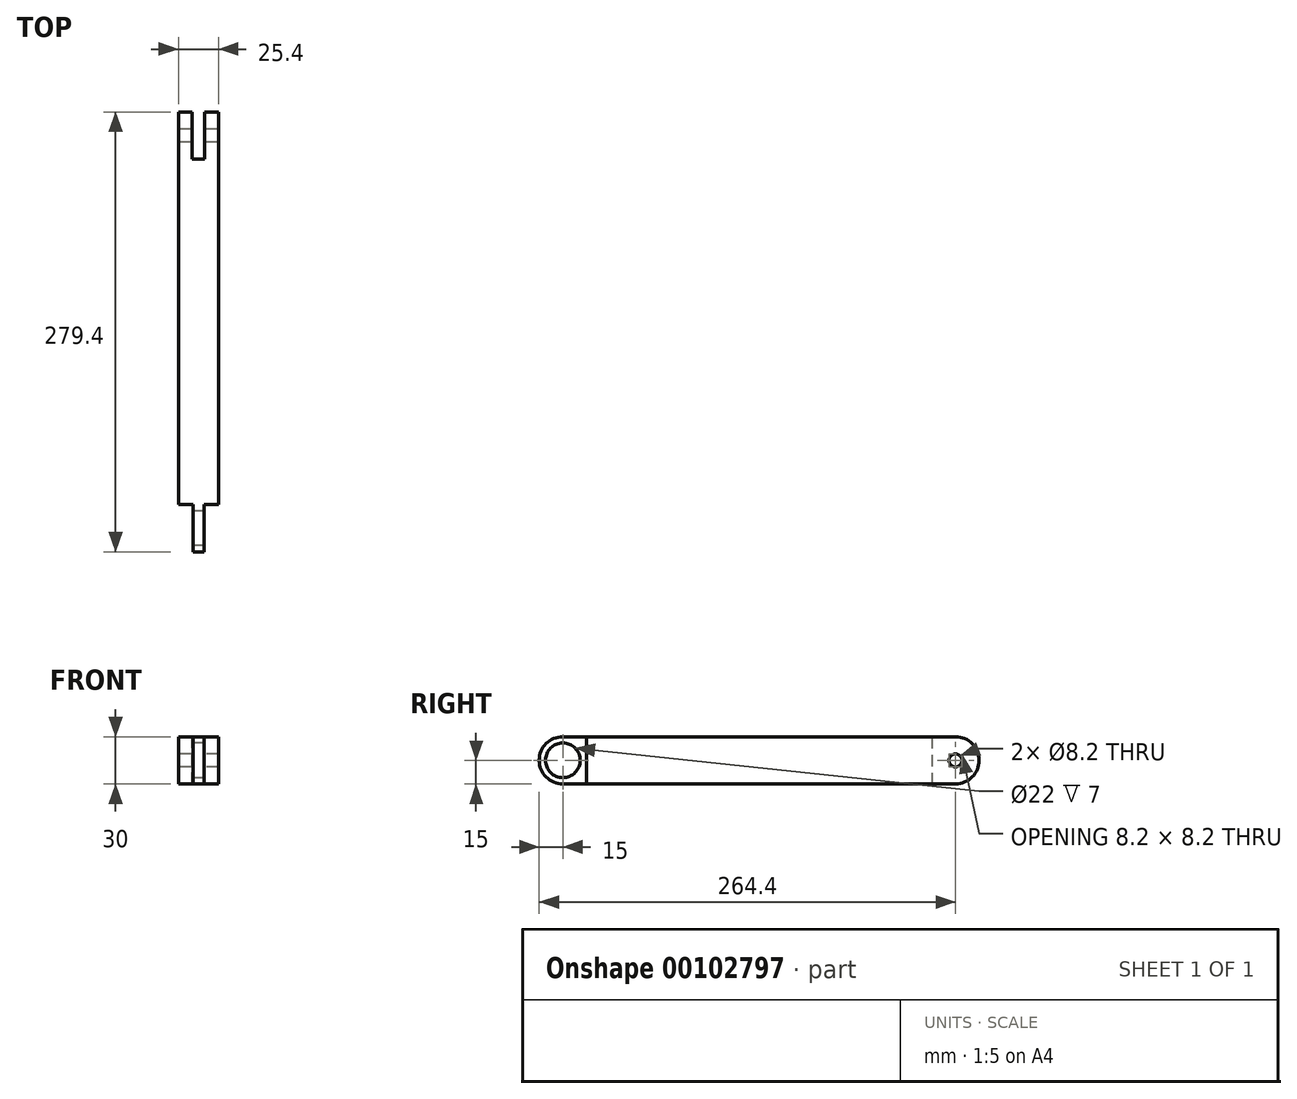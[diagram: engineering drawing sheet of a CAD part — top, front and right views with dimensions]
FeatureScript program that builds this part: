
annotation { "Feature Type Name" : "Feature", "Feature Type Description" : "" }
export const myFeature = defineFeature(function(context is Context, id is Id, definition is map)
    precondition{}
    {
        {
            var Q0;
            Q0=qCreatedBy(makeId("Top.planeOp"),FACE);
            var sketch = newSketch(context, id + "F0", { "sketchPlane" : qUnion([Q0])});
            skLineSegment(sketch, "E0", {"start": v(-12.7, 124.7) * mm, "end": v(-4, 124.7) * mm});
            skLineSegment(sketch, "E1", {"start": v(-4, 124.7) * mm, "end": v(-4, 94.7) * mm});
            skLineSegment(sketch, "E2", {"start": v(-4, 94.7) * mm, "end": v(4, 94.7) * mm});
            skLineSegment(sketch, "E3", {"start": v(4, 94.7) * mm, "end": v(4, 124.7) * mm});
            skLineSegment(sketch, "E4", {"start": v(4, 124.7) * mm, "end": v(12.7, 124.7) * mm});
            skLineSegment(sketch, "E5", {"start": v(12.7, 124.7) * mm, "end": v(12.7, -124.7) * mm});
            skLineSegment(sketch, "E6", {"start": v(12.7, -124.7) * mm, "end": v(3.5, -124.7) * mm});
            skLineSegment(sketch, "E7", {"start": v(3.5, -124.7) * mm, "end": v(3.5, -154.7) * mm});
            skLineSegment(sketch, "E8", {"start": v(3.5, -154.7) * mm, "end": v(-3.5, -154.7) * mm});
            skLineSegment(sketch, "E9", {"start": v(-3.5, -154.7) * mm, "end": v(-3.5, -124.7) * mm});
            skLineSegment(sketch, "E10", {"start": v(-3.5, -124.7) * mm, "end": v(-12.7, -124.7) * mm});
            skLineSegment(sketch, "E11", {"start": v(-12.7, -124.7) * mm, "end": v(-12.7, 124.7) * mm});
            skLineSegment(sketch, "E12", {"start": v(-4, 124.7) * mm, "end": v(4, 124.7) * mm, "construction": true});
            skPoint(sketch, "E13", {"position": v(12.7, 0) * mm});
            skPoint(sketch, "E14", {"position": v(0, 124.7) * mm});
            skSolve(sketch);
        }
        {
            var Q0;
            Q0=makeQuery(id+"F0.imprint","IMPRINT",FACE,{"disambiguationData":[TD([[makeQuery(id+"F0.imprint","IMPRINT",EDGE,{"derivedFrom":sQuery(id+"F0.wireOp",EDGE,"E0")}),-1.0]])]});
            extrude(context, id + "F1", {"entities" : qUnion([Q0]), "depth" : 30 * mm});
        }
        {
            var Q0;
            Q0=makeQuery(id+"F1.opExtrude","SWEPT_FACE",FACE,{"disambiguationData":[OSD([sQuery(id+"F0.wireOp",EDGE,"E11")])]});
            var sketch = newSketch(context, id + "F2", { "sketchPlane" : qUnion([Q0])});
            skLineSegment(sketch, "E15.0.0", {"start": v(124.7, 0) * mm, "end": v(154.7, 0) * mm});
            skLineSegment(sketch, "E15.0.1", {"start": v(154.7, 0) * mm, "end": v(154.7, 30) * mm});
            skLineSegment(sketch, "E15.0.2", {"start": v(154.7, 30) * mm, "end": v(124.7, 30) * mm});
            skLineSegment(sketch, "E15.0.3", {"start": v(124.7, 30) * mm, "end": v(124.7, 0) * mm});
            skPoint(sketch, "E16", {"position": v(139.7, 15) * mm});
            skPoint(sketch, "E16.positionSnap0", {"position": v(154.7, 15) * mm});
            skPoint(sketch, "E16.positionSnap1", {"position": v(139.7, 30) * mm});
            skLineSegment(sketch, "E17.0.0", {"start": v(-94.7, 0) * mm, "end": v(-124.7, 0) * mm});
            skLineSegment(sketch, "E17.0.1", {"start": v(-124.7, 0) * mm, "end": v(-124.7, 30) * mm});
            skLineSegment(sketch, "E17.0.2", {"start": v(-124.7, 30) * mm, "end": v(-94.7, 30) * mm});
            skLineSegment(sketch, "E17.0.3", {"start": v(-94.7, 30) * mm, "end": v(-94.7, 0) * mm});
            skPoint(sketch, "E18", {"position": v(-109.7, 15) * mm});
            skPoint(sketch, "E18.positionSnap0", {"position": v(-109.7, 30) * mm});
            skPoint(sketch, "E18.positionSnap1", {"position": v(-94.7, 15) * mm});
            skCircle(sketch, "E19", {"center": v(-109.7, 15) * mm, "radius": 4.1 * mm});
            skCircle(sketch, "E20", {"center": v(139.7, 15) * mm, "radius": 11 * mm});
            skArc(sketch, "E21", {"start": v(-109.7, 0) * mm, "mid": v(-124.7, 15) * mm, "end": v(-109.7, 30) * mm});
            skArc(sketch, "E22", {"start": v(139.7, 30) * mm, "mid": v(154.7, 15) * mm, "end": v(139.7, 0) * mm});
            skSolve(sketch);
        }
        {
            var Q0;
            {var subQ0=sQuery(id+"F2.wireOp",EDGE,"E15.0.2");var subQ1=sQuery(id+"F2.wireOp",EDGE,"E15.0.1");var subQ2=makeQuery(id+"F2.imprint","INTERSECT",VERTEX,{"derivedFrom":[subQ1,subQ0]});Q0=makeQuery(id+"F2.imprint","IMPRINT",FACE,{"disambiguationData":[TD([[makeQuery(id+"F2.imprint","IMPRINT",EDGE,{"disambiguationData":[TD([[subQ2,1.0]])],"derivedFrom":subQ1}),1.0]])]});}
            var Q1;
            {var subQ0=sQuery(id+"F2.wireOp",EDGE,"E15.0.1");var subQ1=sQuery(id+"F2.wireOp",EDGE,"E15.0.0");var subQ2=makeQuery(id+"F2.imprint","INTERSECT",VERTEX,{"derivedFrom":[subQ1,subQ0]});Q1=makeQuery(id+"F2.imprint","IMPRINT",FACE,{"disambiguationData":[TD([[makeQuery(id+"F2.imprint","IMPRINT",EDGE,{"disambiguationData":[TD([[subQ2,1.0]])],"derivedFrom":subQ1}),1.0]])]});}
            var Q2;
            Q2=makeQuery(id+"F2.imprint","IMPRINT",FACE,{"disambiguationData":[TD([[makeQuery(id+"F2.imprint","IMPRINT",EDGE,{"derivedFrom":sQuery(id+"F2.wireOp",EDGE,"E20")}),1.0]])]});
            var Q3;
            Q3=makeQuery(id+"F2.imprint","IMPRINT",FACE,{"disambiguationData":[TD([[makeQuery(id+"F2.imprint","IMPRINT",EDGE,{"derivedFrom":sQuery(id+"F2.wireOp",EDGE,"E19")}),1.0]])]});
            var Q4;
            {var subQ0=sQuery(id+"F2.wireOp",EDGE,"E17.0.2");var subQ1=sQuery(id+"F2.wireOp",EDGE,"E17.0.1");var subQ2=makeQuery(id+"F2.imprint","INTERSECT",VERTEX,{"derivedFrom":[subQ1,subQ0]});Q4=makeQuery(id+"F2.imprint","IMPRINT",FACE,{"disambiguationData":[TD([[makeQuery(id+"F2.imprint","IMPRINT",EDGE,{"disambiguationData":[TD([[subQ2,-1.0]])],"derivedFrom":subQ1}),1.0]])]});}
            var Q5;
            {var subQ0=sQuery(id+"F2.wireOp",EDGE,"E17.0.1");var subQ1=sQuery(id+"F2.wireOp",EDGE,"E17.0.0");var subQ2=makeQuery(id+"F2.imprint","INTERSECT",VERTEX,{"derivedFrom":[subQ1,subQ0]});Q5=makeQuery(id+"F2.imprint","IMPRINT",FACE,{"disambiguationData":[TD([[makeQuery(id+"F2.imprint","IMPRINT",EDGE,{"disambiguationData":[TD([[subQ2,1.0]])],"derivedFrom":subQ1}),-1.0]])]});}
            var Q6;
            Q6=makeQuery(id+"F1.opExtrude","SWEPT_FACE",FACE,{"disambiguationData":[OSD([sQuery(id+"F0.wireOp",EDGE,"E5")])]});
            extrude(context, id + "F3", {"entities" : qUnion([Q0, Q1, Q2, Q3, Q4, Q5]), "operationType" : NewBodyOperationType.REMOVE, "endBound" : BoundingType.UP_TO_SURFACE, "oppositeDirection" : true, "endBoundEntityFace" : qUnion([Q6]), "depth" : 25 * mm});
        }
    });
